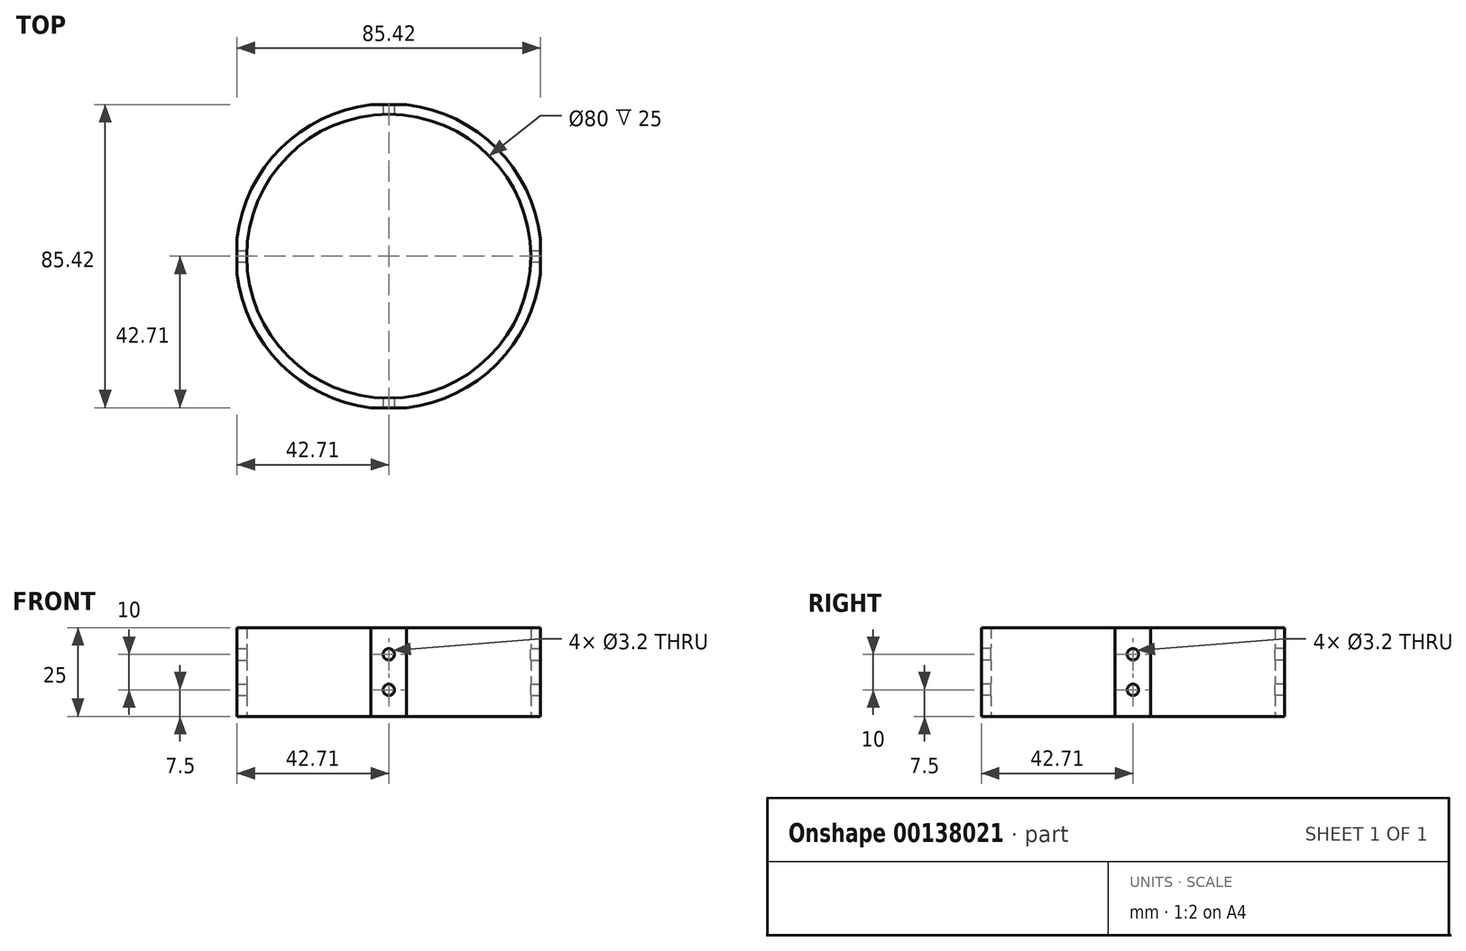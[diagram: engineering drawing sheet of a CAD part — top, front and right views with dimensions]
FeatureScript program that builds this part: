
annotation { "Feature Type Name" : "Feature", "Feature Type Description" : "" }
export const myFeature = defineFeature(function(context is Context, id is Id, definition is map)
    precondition{}
    {
        {
            var Q0;
            Q0=qCreatedBy(makeId("Top.planeOp"),FACE);
            var sketch = newSketch(context, id + "F0", { "sketchPlane" : qUnion([Q0])});
            skCircle(sketch, "E0", {"center": v(0, 0) * mm, "radius": 43 * mm});
            skCircle(sketch, "E1.0", {"center": v(0, 0) * mm, "radius": 40 * mm});
            skLineSegment(sketch, "E2", {"start": v(42.7, 5) * mm, "end": v(42.7, -5) * mm});
            skLineSegment(sketch, "E3", {"start": v(-42.7, 5) * mm, "end": v(-42.7, -5) * mm});
            skLineSegment(sketch, "E4", {"start": v(42.7, 0) * mm, "end": v(-42.7, 0) * mm, "construction": true});
            skLineSegment(sketch, "E5", {"start": v(-5, 42.7) * mm, "end": v(5, 42.7) * mm});
            skLineSegment(sketch, "E6", {"start": v(-5, -42.7) * mm, "end": v(5, -42.7) * mm});
            skLineSegment(sketch, "E7", {"start": v(0, -42.7) * mm, "end": v(0, 42.7) * mm, "construction": true});
            skSolve(sketch);
        }
        {
            var Q0;
            Q0=makeQuery(id+"F0.imprint","IMPRINT",FACE,{"disambiguationData":[TD([[makeQuery(id+"F0.imprint","IMPRINT",EDGE,{"derivedFrom":sQuery(id+"F0.wireOp",EDGE,"E0")}),1.0]])]});
            extrude(context, id + "F1", {"entities" : qUnion([Q0]), "depth" : 25 * mm});
        }
        {
            var Q0;
            Q0=makeQuery(id+"F1.opExtrude","SWEPT_FACE",FACE,{"disambiguationData":[OSD([sQuery(id+"F0.wireOp",EDGE,"E2")])]});
            var sketch = newSketch(context, id + "F2", { "sketchPlane" : qUnion([Q0])});
            skLineSegment(sketch, "E8", {"start": v(0, 25) * mm, "end": v(0, 0) * mm, "construction": true});
            skCircle(sketch, "E9", {"center": v(0, 17.5) * mm, "radius": 1.6 * mm});
            skCircle(sketch, "E10", {"center": v(0, 7.5) * mm, "radius": 1.6 * mm});
            skSolve(sketch);
        }
        {
            var Q0;
            Q0=makeQuery(id+"F2.imprint","IMPRINT",FACE,{"disambiguationData":[TD([[makeQuery(id+"F2.imprint","IMPRINT",EDGE,{"derivedFrom":sQuery(id+"F2.wireOp",EDGE,"E9")}),1.0]])]});
            var Q1;
            Q1=makeQuery(id+"F2.imprint","IMPRINT",FACE,{"disambiguationData":[TD([[makeQuery(id+"F2.imprint","IMPRINT",EDGE,{"derivedFrom":sQuery(id+"F2.wireOp",EDGE,"E10")}),1.0]])]});
            extrude(context, id + "F3", {"entities" : qUnion([Q0, Q1]), "operationType" : NewBodyOperationType.REMOVE, "endBound" : BoundingType.THROUGH_ALL, "oppositeDirection" : true, "depth" : 25 * mm});
        }
        {
            var Q0;
            Q0=makeQuery(id+"F1.opExtrude","SWEPT_FACE",FACE,{"disambiguationData":[OSD([sQuery(id+"F0.wireOp",EDGE,"E6")])]});
            var sketch = newSketch(context, id + "F4", { "sketchPlane" : qUnion([Q0])});
            skLineSegment(sketch, "E11", {"start": v(0, 25) * mm, "end": v(0, 0) * mm, "construction": true});
            skCircle(sketch, "E12", {"center": v(0, 17.5) * mm, "radius": 1.6 * mm});
            skCircle(sketch, "E13", {"center": v(0, 7.5) * mm, "radius": 1.6 * mm});
            skSolve(sketch);
        }
        {
            var Q0;
            Q0=makeQuery(id+"F4.imprint","IMPRINT",FACE,{"disambiguationData":[TD([[makeQuery(id+"F4.imprint","IMPRINT",EDGE,{"derivedFrom":sQuery(id+"F4.wireOp",EDGE,"E12")}),1.0]])]});
            var Q1;
            Q1=makeQuery(id+"F4.imprint","IMPRINT",FACE,{"disambiguationData":[TD([[makeQuery(id+"F4.imprint","IMPRINT",EDGE,{"derivedFrom":sQuery(id+"F4.wireOp",EDGE,"E13")}),1.0]])]});
            extrude(context, id + "F5", {"entities" : qUnion([Q0, Q1]), "operationType" : NewBodyOperationType.REMOVE, "endBound" : BoundingType.THROUGH_ALL, "oppositeDirection" : true, "depth" : 25 * mm});
        }
    });
